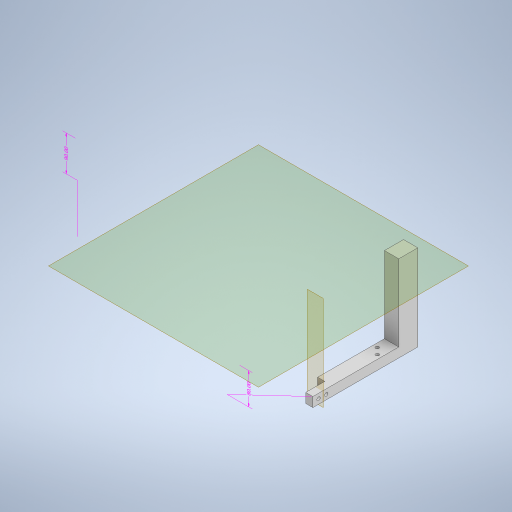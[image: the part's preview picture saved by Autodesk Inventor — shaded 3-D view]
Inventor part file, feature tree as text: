
AUTODESK INVENTOR PART (.ipt)
format: ipt  version: 2023 (Build 270158000, 158)  size: 383,488 bytes
history: native  units: mm
features: sketch x9, extrude x5, other x4, hole x3, plane x2, split x2
ambient origin geometry x8: Origin, YZ Plane, XZ Plane, XY Plane, X Axis, Y Axis, Z Axis, Center Point
bodies: Body1 (feature_tree), Body2 (feature_tree)
feature tree (25):
  other  "Sólido1"
  other  "Anotaciones"
  extrude  "Extrusión1"  Depth=15.0mm
  hole  "Agujero1"  [1 undecoded]
  extrude  "Extrusión2"  Depth=15.0mm
  extrude  "Extrusión3"  Depth=80.0mm TaperAngle=0.0deg
  extrude  "Extrusión4"  Depth=200.0mm
  extrude  "Extrusión5"  Depth=20.0mm
  hole  "Agujero2"  [1 undecoded]
  plane  "Plano de trabajo1"
  split  "Dividir1"
  sketch  "Boceto9"  dims[d37=20.0mm d38=20.0mm]
  plane  "Plano de trabajo2"
  hole  "Agujero3"  [1 undecoded]
  split  "Dividir2"
  sketch  "Boceto2"  dims[d7=15.0mm d8=200.0mm]
  sketch  "Boceto3"  dims[d9=10.0mm d10=0.0mm]
  sketch  "Boceto4"  dims[d12=1.75mm d13=1.75mm d14=1.75mm d15=1.75mm d16=10.0mm d17=10.0mm d19=30.0mm]
  sketch  "Boceto5"  dims[d20=3.5mm d21=6.0mm d22=4.0mm d23=2.0mm d24=90.0deg d25=8.0mm d26=20.594885mm d27=15.0mm]
  sketch  "Boceto6"  dims[d28=20.0mm d29=80.0mm d30=0.0mm]
  sketch  "Boceto7"  dims[d31=48.0mm d32=200.0mm]
  sketch  "Boceto8"  dims[d33=110.0mm d34=0.0mm d36=20.0mm]
  sketch  "Boceto10"  dims[d39=90.0mm d40=0.0mm d42=10.0mm d43=30.0mm d44=0.0mm d46=1.75mm d47=1.75mm d48=1.75mm d49=1.75mm d50=10.0mm d51=10.0mm d52=15.0mm d56=3.5mm d57=6.0mm d58=4.0mm d59=2.0mm d60=90.0deg d61=8.0mm d62=20.594885mm d63=10.0mm d65=10.0mm d66=10.0mm d67=31.75mm d70=15.0mm d74=200.0mm d78=20.0mm d82=90.0deg d83=10.0mm d84=10.0mm d85=3.5mm d86=4.0mm d87=5.0mm d88=3.5mm d89=6.0mm d90=4.0mm d91=2.0mm d92=90.0deg d93=8.0mm d94=20.594885mm d75=1.454734mm d76=6.982969mm d77=80.0mm d79=4.097996mm d80=1.406125mm d81=90.0mm]
  other  "Cota lineal 2"
  other  "Cota lineal 3"
note: 3 required parameter values undecoded (feature->parameter linkage not recoverable at this tier; creation-order binding heuristic only, values carry confidence <= 0.55)
